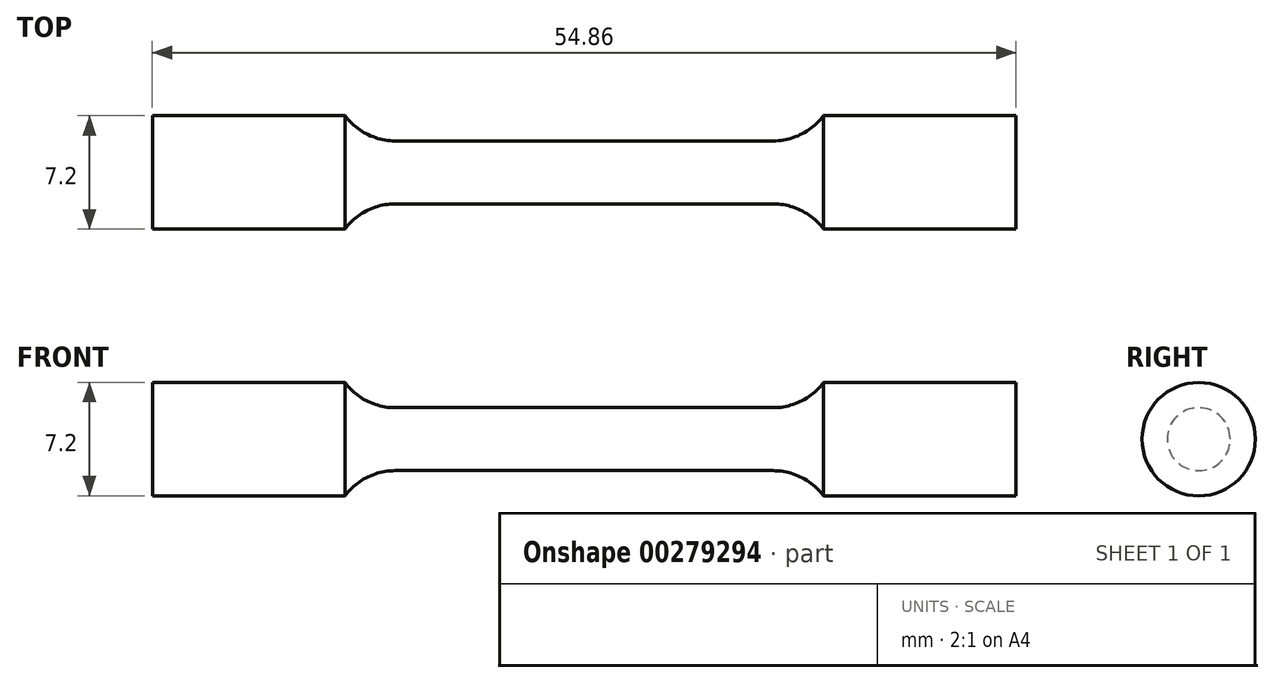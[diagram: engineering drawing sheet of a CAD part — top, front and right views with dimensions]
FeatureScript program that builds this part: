
annotation { "Feature Type Name" : "Feature", "Feature Type Description" : "" }
export const myFeature = defineFeature(function(context is Context, id is Id, definition is map)
    precondition{}
    {
        {
            var Q0;
            Q0=qCreatedBy(makeId("Front.planeOp"),FACE);
            var sketch = newSketch(context, id + "F0", { "sketchPlane" : qUnion([Q0])});
            skLineSegment(sketch, "E0", {"start": v(0, 2) * mm, "end": v(12, 2) * mm});
            skArc(sketch, "E1", {"start": v(12, 2) * mm, "mid": v(13.79, 2.42) * mm, "end": v(15.2, 3.6) * mm});
            skLineSegment(sketch, "E2", {"start": v(15.2, 3.6) * mm, "end": v(27.43, 3.6) * mm});
            skLineSegment(sketch, "E3", {"start": v(27.43, 3.6) * mm, "end": v(27.43, 0) * mm});
            skArc(sketch, "E4.MirrorCS", {"start": v(-12, 2) * mm, "mid": v(-13.79, 2.42) * mm, "end": v(-15.2, 3.6) * mm});
            skLineSegment(sketch, "E5.MirrorCS", {"start": v(0, 2) * mm, "end": v(-12, 2) * mm});
            skLineSegment(sketch, "E6.MirrorCS", {"start": v(-27.43, 3.6) * mm, "end": v(-27.43, 0) * mm});
            skLineSegment(sketch, "E7.MirrorCS", {"start": v(-15.2, 3.6) * mm, "end": v(-27.43, 3.6) * mm});
            skLineSegment(sketch, "E8", {"start": v(-27.43, 0) * mm, "end": v(27.43, 0) * mm});
            skSolve(sketch);
        }
        {
            var Q0;
            Q0 = qSketchRegion(id + "F0", true);
            var Q1;
            Q1=sQuery(id+"F0.wireOp",EDGE,"E8");
            revolve(context, id + "F1", {"entities" : qUnion([Q0]), "axis" : qUnion([Q1]), "revolveType" : RevolveType.FULL});
        }
    });
